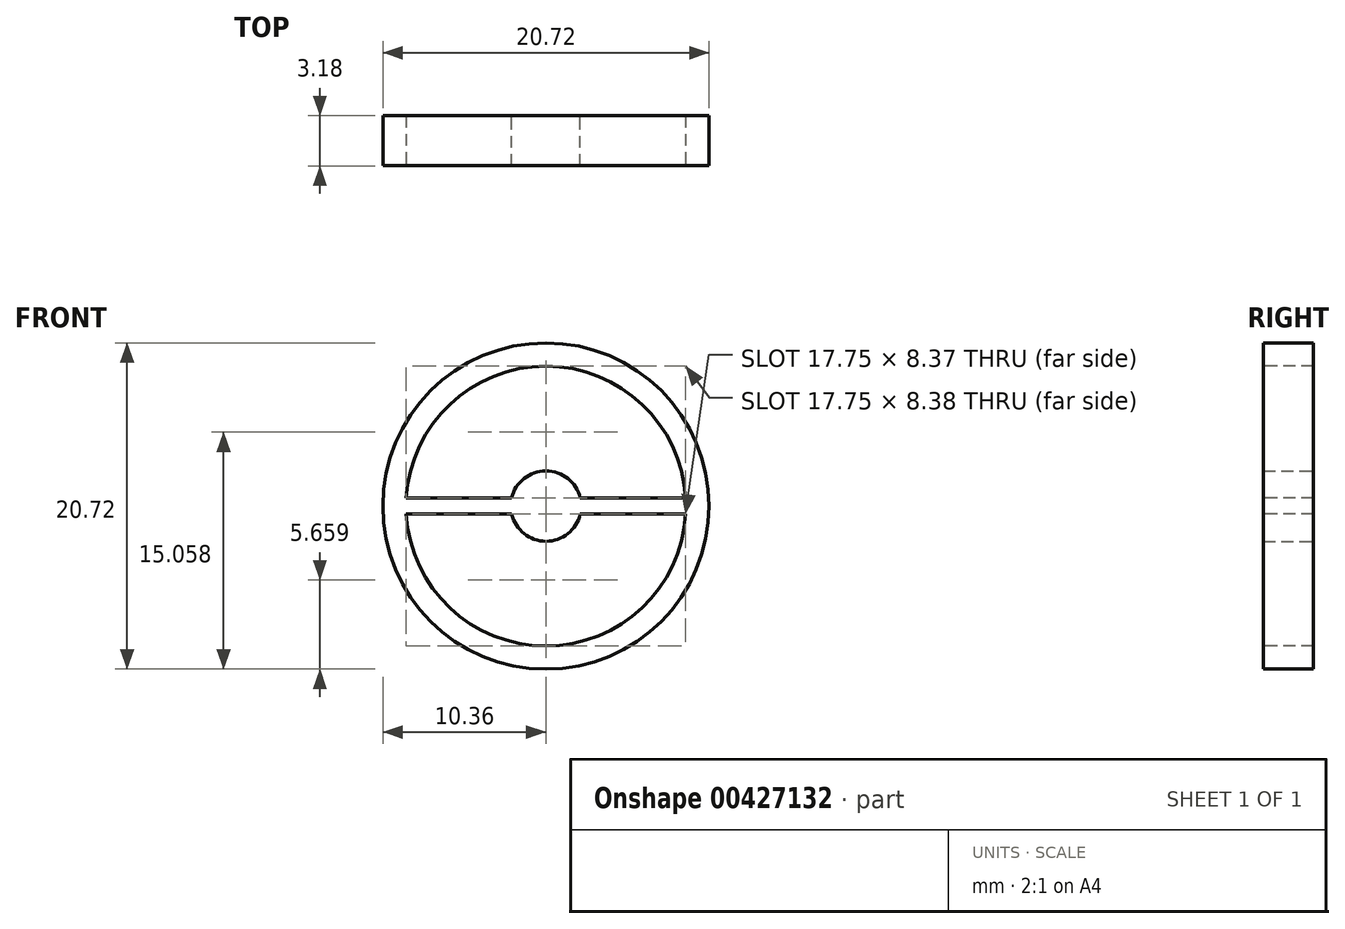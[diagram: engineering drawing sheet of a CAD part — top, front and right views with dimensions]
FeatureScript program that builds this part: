
annotation { "Feature Type Name" : "Feature", "Feature Type Description" : "" }
export const myFeature = defineFeature(function(context is Context, id is Id, definition is map)
    precondition{}
    {
        {
            var Q0;
            Q0=qCreatedBy(makeId("Front.planeOp"),FACE);
            var sketch = newSketch(context, id + "F0", { "sketchPlane" : qUnion([Q0])});
            skCircle(sketch, "E0", {"center": v(0, 0) * mm, "radius": 9.53 * mm});
            skCircle(sketch, "E1", {"center": v(0, 0) * mm, "radius": 2.24 * mm});
            skLineSegment(sketch, "E2", {"start": v(-2.18, 0.5) * mm, "end": v(-9.51, 0.5) * mm});
            skLineSegment(sketch, "E3", {"start": v(-9.51, -0.51) * mm, "end": v(-2.18, -0.51) * mm});
            skLineSegment(sketch, "E4", {"start": v(2.18, 0.5) * mm, "end": v(9.51, 0.5) * mm});
            skLineSegment(sketch, "E5", {"start": v(2.18, -0.51) * mm, "end": v(9.51, -0.51) * mm});
            skCircle(sketch, "E6", {"center": v(0, 0) * mm, "radius": 10.36 * mm});
            skSolve(sketch);
        }
        {
            var Q0;
            Q0=makeQuery(id+"F0.imprint","IMPRINT",FACE,{"disambiguationData":[TD([[makeQuery(id+"F0.imprint","IMPRINT",EDGE,{"derivedFrom":sQuery(id+"F0.wireOp",EDGE,"E6")}),1.0]])]});
            var Q1;
            {var subQ0=sQuery(id+"F0.wireOp",EDGE,"E2");Q1=makeQuery(id+"F0.imprint","IMPRINT",FACE,{"disambiguationData":[TD([[makeQuery(id+"F0.imprint","IMPRINT",EDGE,{"derivedFrom":subQ0}),1.0]])]});}
            var Q2;
            {var subQ0=sQuery(id+"F0.wireOp",EDGE,"E1");var subQ1=makeQuery(id+"F0.imprint","INTERSECT",VERTEX,{"derivedFrom":[subQ0,sQuery(id+"F0.wireOp",EDGE,"E2")]});Q2=makeQuery(id+"F0.imprint","IMPRINT",FACE,{"disambiguationData":[TD([[makeQuery(id+"F0.imprint","IMPRINT",EDGE,{"disambiguationData":[TD([[subQ1,1.0]])],"derivedFrom":subQ0}),1.0]])]});}
            var Q3;
            {var subQ0=sQuery(id+"F0.wireOp",EDGE,"E4");Q3=makeQuery(id+"F0.imprint","IMPRINT",FACE,{"disambiguationData":[TD([[makeQuery(id+"F0.imprint","IMPRINT",EDGE,{"derivedFrom":subQ0}),-1.0]])]});}
            extrude(context, id + "F1", {"entities" : qUnion([Q0, Q1, Q2, Q3]), "depth" : 3.17 * mm});
        }
        {
            var Q0;
            Q0=makeQuery(id+"F1.opExtrude","CAP_FACE",FACE,{"disambiguationData":[OSD([sQuery(id+"F0.wireOp",EDGE,"E0"),sQuery(id+"F0.wireOp",EDGE,"E1"),sQuery(id+"F0.wireOp",EDGE,"E2"),sQuery(id+"F0.wireOp",EDGE,"E3"),sQuery(id+"F0.wireOp",EDGE,"E4"),sQuery(id+"F0.wireOp",EDGE,"E5"),sQuery(id+"F0.wireOp",EDGE,"E6")])],"isStart":false});
            var sketch = newSketch(context, id + "F2", { "sketchPlane" : qUnion([Q0])});
            skCircle(sketch, "E7", {"center": v(0, 0) * mm, "radius": 8.89 * mm});
            skSolve(sketch);
        }
        {
            var Q0;
            {var subQ1=sQuery(id+"F0.wireOp",EDGE,"E3");var subQ7=sQuery(id+"F0.wireOp",EDGE,"E0");var subQ8=makeQuery(id+"F1.opExtrude","CAP_EDGE",EDGE,{"disambiguationData":[OSD([subQ7]),TDD([makeQuery(id+"F0.imprint","IMPRINT",EDGE,{"disambiguationData":[TD([[makeQuery(id+"F0.imprint","INTERSECT",VERTEX,{"derivedFrom":[subQ7,subQ1]}),-1.0]])],"derivedFrom":subQ7})])],"isStart":false});Q0=makeQuery(id+"F2.imprint","IMPRINT",FACE,{"disambiguationData":[TD([[makeQuery(id+"F2.imprint","IMPRINT",EDGE,{"derivedFrom":subQ8}),1.0]])]});}
            var Q1;
            {var subQ1=sQuery(id+"F0.wireOp",EDGE,"E2");var subQ7=sQuery(id+"F0.wireOp",EDGE,"E0");var subQ8=makeQuery(id+"F1.opExtrude","CAP_EDGE",EDGE,{"disambiguationData":[OSD([subQ7]),TDD([makeQuery(id+"F0.imprint","IMPRINT",EDGE,{"disambiguationData":[TD([[makeQuery(id+"F0.imprint","INTERSECT",VERTEX,{"derivedFrom":[subQ7,subQ1]}),1.0]])],"derivedFrom":subQ7})])],"isStart":false});Q1=makeQuery(id+"F2.imprint","IMPRINT",FACE,{"disambiguationData":[TD([[makeQuery(id+"F2.imprint","IMPRINT",EDGE,{"derivedFrom":subQ8}),1.0]])]});}
            extrude(context, id + "F3", {"entities" : qUnion([Q0, Q1]), "operationType" : NewBodyOperationType.ADD, "oppositeDirection" : true, "depth" : 3.17 * mm});
        }
    });
